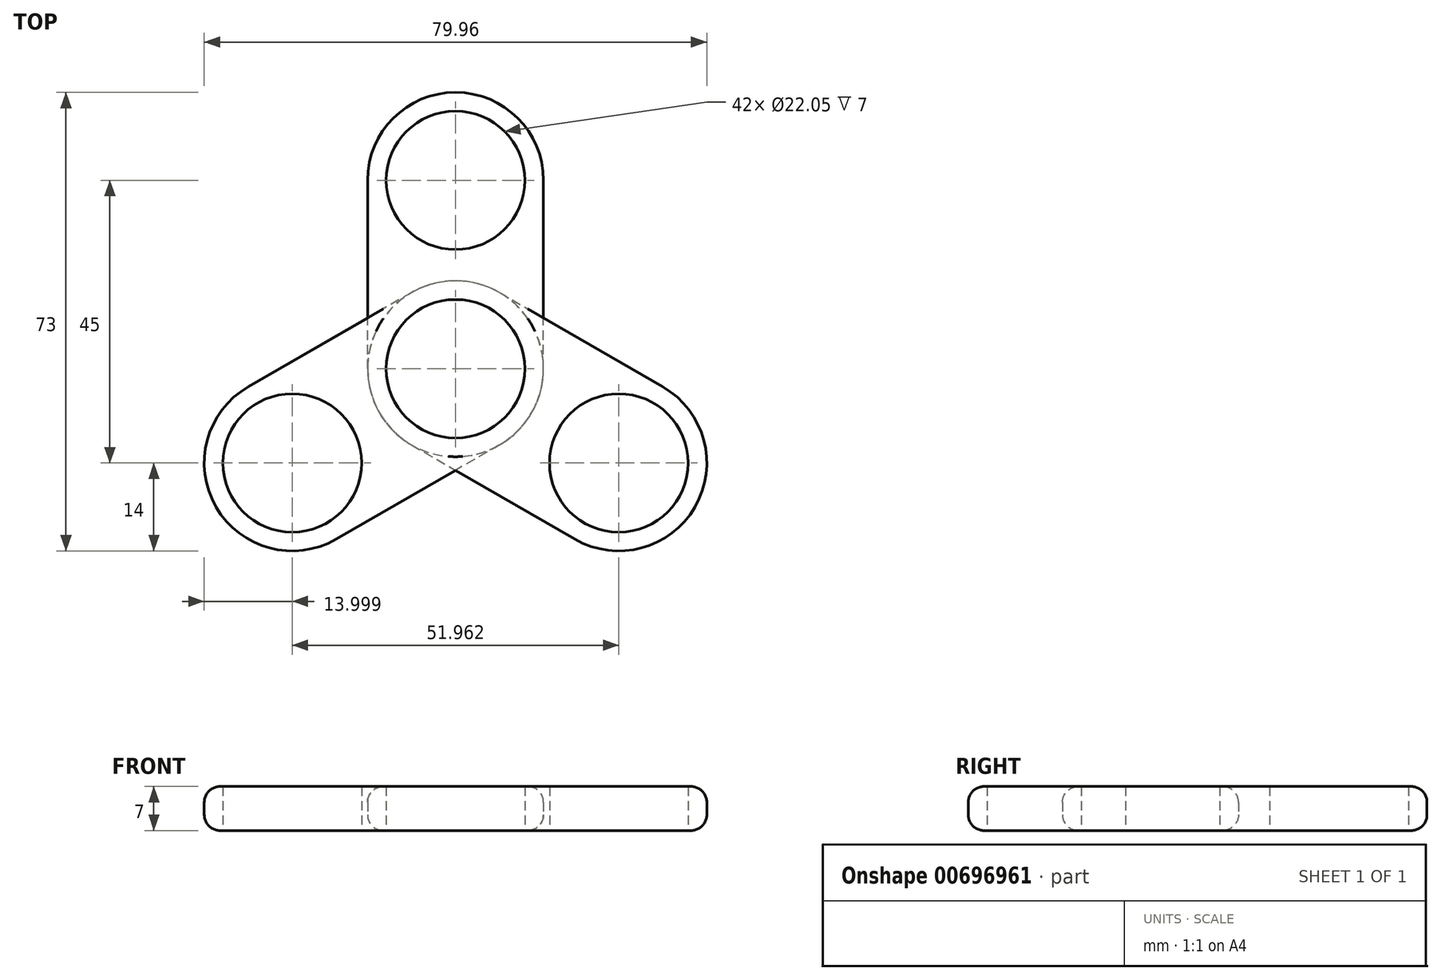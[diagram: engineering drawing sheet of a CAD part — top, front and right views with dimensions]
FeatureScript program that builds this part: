
annotation { "Feature Type Name" : "Feature", "Feature Type Description" : "" }
export const myFeature = defineFeature(function(context is Context, id is Id, definition is map)
    precondition{}
    {
        {
            var Q0;
            Q0=qCreatedBy(makeId("Top.planeOp"),FACE);
            var sketch = newSketch(context, id + "F0", { "sketchPlane" : qUnion([Q0])});
            skLineSegment(sketch, "E0.bottom", {"start": v(14, -15) * mm, "end": v(-14, -15) * mm});
            skLineSegment(sketch, "E0.top", {"start": v(14, 15) * mm, "end": v(-14, 15) * mm});
            skLineSegment(sketch, "E0.left", {"start": v(14, -15) * mm, "end": v(14, 15) * mm});
            skLineSegment(sketch, "E0.right", {"start": v(-14, -15) * mm, "end": v(-14, 15) * mm});
            skPoint(sketch, "E0.middle", {"position": v(0, 0) * mm});
            skCircle(sketch, "E1", {"center": v(0, 15) * mm, "radius": 14 * mm});
            skCircle(sketch, "E2", {"center": v(0, 15) * mm, "radius": 11.03 * mm});
            skCircle(sketch, "E3", {"center": v(0, -15) * mm, "radius": 14 * mm});
            skCircle(sketch, "E4", {"center": v(0, -15) * mm, "radius": 11.03 * mm});
            skSolve(sketch);
        }
        {
            var Q0;
            {var subQ1=sQuery(id+"F0.wireOp",EDGE,"E0.top");var subQ3=sQuery(id+"F0.wireOp",EDGE,"E2");var subQ4=makeQuery(id+"F0.imprint","INTERSECT",VERTEX,{"disambiguationData":[OD(0.0)],"derivedFrom":[subQ1,subQ3]});Q0=makeQuery(id+"F0.imprint","IMPRINT",FACE,{"disambiguationData":[TD([[makeQuery(id+"F0.imprint","IMPRINT",EDGE,{"disambiguationData":[TD([[subQ4,-1.0]])],"derivedFrom":subQ3}),-1.0]])]});}
            var Q1;
            {var subQ1=sQuery(id+"F0.wireOp",EDGE,"E0.top");var subQ3=sQuery(id+"F0.wireOp",EDGE,"E2");var subQ4=makeQuery(id+"F0.imprint","INTERSECT",VERTEX,{"disambiguationData":[OD(0.0)],"derivedFrom":[subQ1,subQ3]});Q1=makeQuery(id+"F0.imprint","IMPRINT",FACE,{"disambiguationData":[TD([[makeQuery(id+"F0.imprint","IMPRINT",EDGE,{"disambiguationData":[TD([[subQ4,1.0]])],"derivedFrom":subQ3}),-1.0]])]});}
            var Q2;
            {var subQ0=sQuery(id+"F0.wireOp",EDGE,"E0.left");Q2=makeQuery(id+"F0.imprint","IMPRINT",FACE,{"disambiguationData":[TD([[makeQuery(id+"F0.imprint","IMPRINT",EDGE,{"derivedFrom":subQ0}),1.0]])]});}
            var Q3;
            {var subQ1=sQuery(id+"F0.wireOp",EDGE,"E0.bottom");var subQ3=sQuery(id+"F0.wireOp",EDGE,"E4");var subQ4=makeQuery(id+"F0.imprint","INTERSECT",VERTEX,{"disambiguationData":[OD(0.0)],"derivedFrom":[subQ1,subQ3]});Q3=makeQuery(id+"F0.imprint","IMPRINT",FACE,{"disambiguationData":[TD([[makeQuery(id+"F0.imprint","IMPRINT",EDGE,{"disambiguationData":[TD([[subQ4,-1.0]])],"derivedFrom":subQ3}),-1.0]])]});}
            var Q4;
            {var subQ1=sQuery(id+"F0.wireOp",EDGE,"E0.bottom");var subQ3=sQuery(id+"F0.wireOp",EDGE,"E4");var subQ4=makeQuery(id+"F0.imprint","INTERSECT",VERTEX,{"disambiguationData":[OD(0.0)],"derivedFrom":[subQ1,subQ3]});Q4=makeQuery(id+"F0.imprint","IMPRINT",FACE,{"disambiguationData":[TD([[makeQuery(id+"F0.imprint","IMPRINT",EDGE,{"disambiguationData":[TD([[subQ4,1.0]])],"derivedFrom":subQ3}),-1.0]])]});}
            extrude(context, id + "F1", {"entities" : qUnion([Q0, Q1, Q2, Q3, Q4]), "depth" : 7 * mm, "offsetDistance" : 25 * mm});
        }
        {
            var Q0;
            Q0=makeQuery(id+"F1.opExtrude","SWEPT_BODY",BODY,{"disambiguationData":[OSD([sQuery(id+"F0.wireOp",EDGE,"E0.left"),sQuery(id+"F0.wireOp",EDGE,"E0.right"),sQuery(id+"F0.wireOp",EDGE,"E1"),sQuery(id+"F0.wireOp",EDGE,"E2"),sQuery(id+"F0.wireOp",EDGE,"E3"),sQuery(id+"F0.wireOp",EDGE,"E4")])]});
            var Q1;
            Q1=makeQuery(id+"F1.opExtrude","SWEPT_FACE",FACE,{"disambiguationData":[OSD([sQuery(id+"F0.wireOp",EDGE,"E3")])]});
            circularPattern(context, id + "F2", {"entities" : qUnion([Q0]), "axis" : qUnion([Q1]), "angle" : 360 * degree, "instanceCount" : 3, "equalSpace" : true});
        }
        {
            var Q0;
            Q0=makeQuery(id+"F1.opExtrude","CAP_EDGE",EDGE,{"disambiguationData":[OSD([sQuery(id+"F0.wireOp",EDGE,"E0.right")])],"isStart":false});
            var Q1;
            Q1=makeQuery(id+"F1.opExtrude","CAP_EDGE",EDGE,{"disambiguationData":[OSD([sQuery(id+"F0.wireOp",EDGE,"E1")])],"isStart":false});
            var Q2;
            Q2=makeQuery(id+"F1.opExtrude","CAP_EDGE",EDGE,{"disambiguationData":[OSD([sQuery(id+"F0.wireOp",EDGE,"E0.left")])],"isStart":false});
            var Q3;
            Q3=makeQuery(id+"F2.opPattern","COPY",EDGE,{"derivedFrom":makeQuery(id+"F1.opExtrude","CAP_EDGE",EDGE,{"disambiguationData":[OSD([sQuery(id+"F0.wireOp",EDGE,"E0.right")])],"isStart":false}),"instanceName":"1"});
            var Q4;
            Q4=makeQuery(id+"F2.opPattern","COPY",EDGE,{"derivedFrom":makeQuery(id+"F1.opExtrude","CAP_EDGE",EDGE,{"disambiguationData":[OSD([sQuery(id+"F0.wireOp",EDGE,"E1")])],"isStart":false}),"instanceName":"1"});
            var Q5;
            Q5=makeQuery(id+"F2.opPattern","COPY",EDGE,{"derivedFrom":makeQuery(id+"F1.opExtrude","CAP_EDGE",EDGE,{"disambiguationData":[OSD([sQuery(id+"F0.wireOp",EDGE,"E0.left")])],"isStart":false}),"instanceName":"1"});
            var Q6;
            Q6=makeQuery(id+"F2.opPattern","COPY",EDGE,{"derivedFrom":makeQuery(id+"F1.opExtrude","CAP_EDGE",EDGE,{"disambiguationData":[OSD([sQuery(id+"F0.wireOp",EDGE,"E0.right")])],"isStart":false}),"instanceName":"2"});
            var Q7;
            Q7=makeQuery(id+"F2.opPattern","COPY",EDGE,{"derivedFrom":makeQuery(id+"F1.opExtrude","CAP_EDGE",EDGE,{"disambiguationData":[OSD([sQuery(id+"F0.wireOp",EDGE,"E1")])],"isStart":false}),"instanceName":"2"});
            var Q8;
            Q8=makeQuery(id+"F2.opPattern","COPY",EDGE,{"derivedFrom":makeQuery(id+"F1.opExtrude","CAP_EDGE",EDGE,{"disambiguationData":[OSD([sQuery(id+"F0.wireOp",EDGE,"E0.left")])],"isStart":false}),"instanceName":"2"});
            var Q9;
            Q9=makeQuery(id+"F2.opPattern","COPY",EDGE,{"derivedFrom":makeQuery(id+"F1.opExtrude","CAP_EDGE",EDGE,{"disambiguationData":[OSD([sQuery(id+"F0.wireOp",EDGE,"E0.right")])],"isStart":true}),"instanceName":"1"});
            var Q10;
            Q10=makeQuery(id+"F2.opPattern","COPY",EDGE,{"derivedFrom":makeQuery(id+"F1.opExtrude","CAP_EDGE",EDGE,{"disambiguationData":[OSD([sQuery(id+"F0.wireOp",EDGE,"E0.right")])],"isStart":true}),"instanceName":"2"});
            var Q11;
            Q11=makeQuery(id+"F1.opExtrude","CAP_EDGE",EDGE,{"disambiguationData":[OSD([sQuery(id+"F0.wireOp",EDGE,"E1")])],"isStart":true});
            fillet(context, id + "F3", {"entities" : qUnion([Q0, Q1, Q2, Q3, Q4, Q5, Q6, Q7, Q8, Q9, Q10, Q11]), "radius" : 2.5 * mm, "tangentPropagation" : true, "allowEdgeOverflow" : false});
        }
    });
